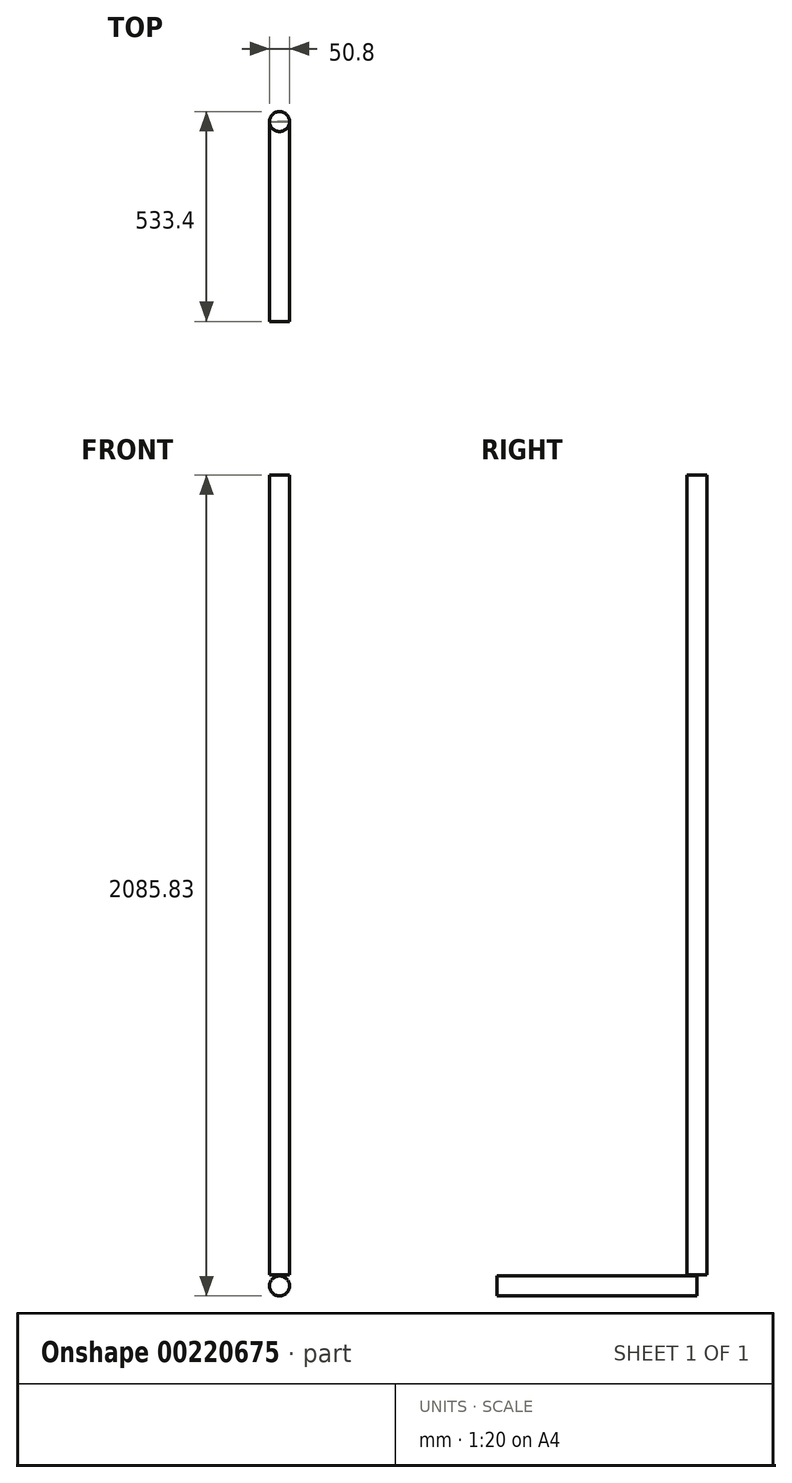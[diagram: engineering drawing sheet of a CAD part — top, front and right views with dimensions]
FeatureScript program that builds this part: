
annotation { "Feature Type Name" : "Feature", "Feature Type Description" : "" }
export const myFeature = defineFeature(function(context is Context, id is Id, definition is map)
    precondition{}
    {
        {
            var Q0;
            Q0=qCreatedBy(makeId("Top.planeOp"),FACE);
            var sketch = newSketch(context, id + "F0", { "sketchPlane" : qUnion([Q0])});
            skCircle(sketch, "E0", {"center": v(0, 0) * mm, "radius": 25.4 * mm});
            skSolve(sketch);
        }
        {
            var Q0;
            Q0 = qSketchRegion(id + "F0", true);
            extrude(context, id + "F1", {"entities" : qUnion([Q0]), "depth" : 2032 * mm});
        }
        {
            var Q0;
            Q0=qCreatedBy(makeId("Front.planeOp"),FACE);
            var sketch = newSketch(context, id + "F2", { "sketchPlane" : qUnion([Q0])});
            skCircle(sketch, "E1", {"center": v(0, -28.43) * mm, "radius": 25.4 * mm});
            skSolve(sketch);
        }
        {
            var Q0;
            Q0=makeQuery(id+"F2.imprint","IMPRINT",FACE,{"disambiguationData":[TD([[makeQuery(id+"F2.imprint","IMPRINT",EDGE,{"derivedFrom":sQuery(id+"F2.wireOp",EDGE,"E1")}),1.0]])]});
            extrude(context, id + "F3", {"entities" : qUnion([Q0]), "depth" : 508 * mm});
        }
    });
